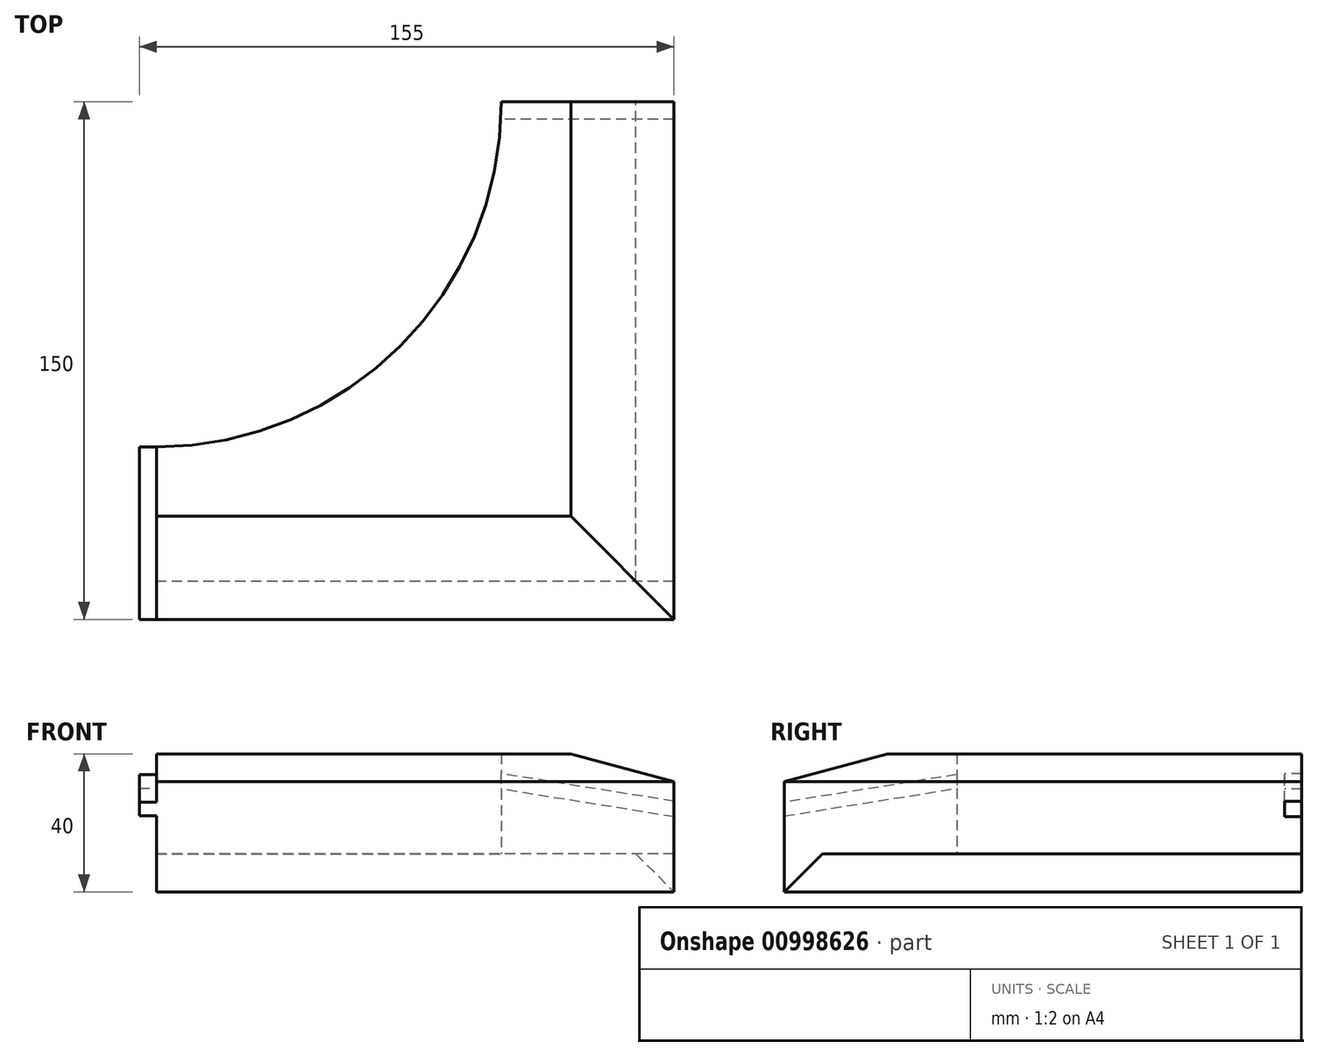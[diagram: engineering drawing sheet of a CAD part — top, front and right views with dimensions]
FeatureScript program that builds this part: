
annotation { "Feature Type Name" : "Feature", "Feature Type Description" : "" }
export const myFeature = defineFeature(function(context is Context, id is Id, definition is map)
    precondition{}
    {
        {
            var Q0;
            Q0=qCreatedBy(makeId("Top.planeOp"),FACE);
            var sketch = newSketch(context, id + "F0", { "sketchPlane" : qUnion([Q0])});
            skLineSegment(sketch, "E0", {"start": v(150, 0) * mm, "end": v(150, -150) * mm});
            skLineSegment(sketch, "E1", {"start": v(150, -150) * mm, "end": v(0, -150) * mm});
            skLineSegment(sketch, "E2", {"start": v(150, 0) * mm, "end": v(100, 0) * mm});
            skLineSegment(sketch, "E3", {"start": v(0, -150) * mm, "end": v(0, -100) * mm});
            skArc(sketch, "E4", {"start": v(0, -100) * mm, "mid": v(70.71, -70.71) * mm, "end": v(100, 0) * mm});
            skSolve(sketch);
        }
        {
            var Q0;
            Q0=makeQuery(id+"F0.imprint","IMPRINT",FACE,{"disambiguationData":[TD([[makeQuery(id+"F0.imprint","IMPRINT",EDGE,{"derivedFrom":sQuery(id+"F0.wireOp",EDGE,"E0")}),-1.0]])]});
            extrude(context, id + "F1", {"entities" : qUnion([Q0]), "depth" : 29 * mm, "offsetDistance" : 25 * mm});
        }
        {
            var Q0;
            Q0=makeQuery(id+"F1.opExtrude","SWEPT_FACE",FACE,{"disambiguationData":[OSD([sQuery(id+"F0.wireOp",EDGE,"E3")])]});
            var sketch = newSketch(context, id + "F2", { "sketchPlane" : qUnion([Q0])});
            skLineSegment(sketch, "E5", {"start": v(120.14, 29) * mm, "end": v(150, 21) * mm});
            skLineSegment(sketch, "E6", {"start": v(150, 21) * mm, "end": v(150, 29) * mm});
            skLineSegment(sketch, "E7", {"start": v(150, 29) * mm, "end": v(120.14, 29) * mm});
            skSolve(sketch);
        }
        {
            var Q0;
            Q0 = qSketchRegion(id + "F2", true);
            extrude(context, id + "F3", {"entities" : qUnion([Q0]), "operationType" : NewBodyOperationType.REMOVE, "endBound" : BoundingType.UP_TO_NEXT, "oppositeDirection" : true, "depth" : 25 * mm, "offsetDistance" : 25 * mm});
        }
        {
            var Q0;
            Q0=makeQuery(id+"F1.opExtrude","SWEPT_FACE",FACE,{"disambiguationData":[OSD([sQuery(id+"F0.wireOp",EDGE,"E2")])]});
            var sketch = newSketch(context, id + "F4", { "sketchPlane" : qUnion([Q0])});
            skLineSegment(sketch, "E8", {"start": v(-150, 29) * mm, "end": v(-120.14, 29) * mm});
            skLineSegment(sketch, "E9", {"start": v(-120.14, 29) * mm, "end": v(-150, 21) * mm});
            skLineSegment(sketch, "E10", {"start": v(-150, 21) * mm, "end": v(-150, 29) * mm});
            skSolve(sketch);
        }
        {
            var Q0;
            Q0 = qSketchRegion(id + "F4", true);
            extrude(context, id + "F5", {"entities" : qUnion([Q0]), "operationType" : NewBodyOperationType.REMOVE, "endBound" : BoundingType.THROUGH_ALL, "oppositeDirection" : true, "depth" : 25 * mm, "offsetDistance" : 25 * mm});
        }
        {
            var Q0;
            Q0=makeQuery(id+"F1.opExtrude","SWEPT_FACE",FACE,{"disambiguationData":[OSD([sQuery(id+"F0.wireOp",EDGE,"E3")])]});
            var sketch = newSketch(context, id + "F6", { "sketchPlane" : qUnion([Q0])});
            skLineSegment(sketch, "E11", {"start": v(100, 23) * mm, "end": v(150, 15) * mm});
            skPoint(sketch, "E11.endSnap0", {"position": v(150, 11) * mm});
            skPoint(sketch, "E11.endSnap1", {"position": v(100, 15) * mm});
            skLineSegment(sketch, "E12", {"start": v(150, 15) * mm, "end": v(150, 11) * mm});
            skLineSegment(sketch, "E13", {"start": v(150, 11) * mm, "end": v(100, 19) * mm});
            skLineSegment(sketch, "E14", {"start": v(100, 19) * mm, "end": v(100, 23) * mm});
            skSolve(sketch);
        }
        {
            var Q0;
            Q0 = qSketchRegion(id + "F6", true);
            extrude(context, id + "F7", {"entities" : qUnion([Q0]), "operationType" : NewBodyOperationType.ADD, "depth" : 5 * mm, "offsetDistance" : 25 * mm});
        }
        {
            var Q0;
            Q0=makeQuery(id+"F1.opExtrude","SWEPT_FACE",FACE,{"disambiguationData":[OSD([sQuery(id+"F0.wireOp",EDGE,"E2")])]});
            var sketch = newSketch(context, id + "F8", { "sketchPlane" : qUnion([Q0])});
            skLineSegment(sketch, "E15", {"start": v(-100, 23.25) * mm, "end": v(-150, 15.25) * mm});
            skLineSegment(sketch, "E16", {"start": v(-100, 18.75) * mm, "end": v(-150, 10.75) * mm});
            skLineSegment(sketch, "E17", {"start": v(-150, 10.75) * mm, "end": v(-150, 15.25) * mm});
            skLineSegment(sketch, "E18", {"start": v(-100, 23.25) * mm, "end": v(-95.06, 24.04) * mm});
            skLineSegment(sketch, "E19", {"start": v(-100, 18.75) * mm, "end": v(-95.06, 19.54) * mm});
            skLineSegment(sketch, "E20", {"start": v(-95.06, 19.54) * mm, "end": v(-95.06, 24.04) * mm});
            skSolve(sketch);
        }
        {
            var Q0;
            Q0 = qSketchRegion(id + "F8", true);
            extrude(context, id + "F9", {"entities" : qUnion([Q0]), "operationType" : NewBodyOperationType.REMOVE, "oppositeDirection" : true, "depth" : 5 * mm, "offsetDistance" : 25 * mm});
        }
        {
            var Q0;
            {var subQ2=sQuery(id+"F0.wireOp",EDGE,"E3");Q0=makeQuery(id+"F7.boolean.opBoolean","SPLIT",FACE,{"disambiguationData":[TD([makeQuery(id+"F7.opExtrude","SWEPT_FACE",FACE,{"disambiguationData":[OSD([sQuery(id+"F6.wireOp",EDGE,"E13")])]})])],"derivedFrom":makeQuery(id+"F1.opExtrude","SWEPT_FACE",FACE,{"disambiguationData":[OSD([subQ2])]})});}
            var sketch = newSketch(context, id + "F10", { "sketchPlane" : qUnion([Q0])});
            skLineSegment(sketch, "E21", {"start": v(150, 0) * mm, "end": v(139, 0) * mm});
            skLineSegment(sketch, "E22", {"start": v(150, 0) * mm, "end": v(150, -11) * mm});
            skLineSegment(sketch, "E23", {"start": v(150, -11) * mm, "end": v(139, 0) * mm});
            skSolve(sketch);
        }
        {
            var Q0;
            Q0=makeQuery(id+"F10.imprint","IMPRINT",FACE,{"disambiguationData":[TD([[makeQuery(id+"F10.imprint","IMPRINT",EDGE,{"derivedFrom":sQuery(id+"F10.wireOp",EDGE,"E21")}),1.0]])]});
            extrude(context, id + "F11", {"entities" : qUnion([Q0]), "operationType" : NewBodyOperationType.ADD, "oppositeDirection" : true, "depth" : 150 * mm, "offsetDistance" : 25 * mm});
        }
        {
            var Q0;
            {var subQ2=sQuery(id+"F0.wireOp",EDGE,"E2");Q0=makeQuery(id+"F9.boolean.opBoolean","SPLIT",FACE,{"disambiguationData":[TD([makeQuery(id+"F9.opExtrude","SWEPT_FACE",FACE,{"disambiguationData":[OSD([sQuery(id+"F8.wireOp",EDGE,"E16"),sQuery(id+"F8.wireOp",EDGE,"E19")])]})])],"derivedFrom":makeQuery(id+"F1.opExtrude","SWEPT_FACE",FACE,{"disambiguationData":[OSD([subQ2])]})});}
            var sketch = newSketch(context, id + "F12", { "sketchPlane" : qUnion([Q0])});
            skLineSegment(sketch, "E24", {"start": v(-150, 0) * mm, "end": v(-150, -11) * mm});
            skLineSegment(sketch, "E25", {"start": v(-150, 0) * mm, "end": v(-139, 0) * mm});
            skLineSegment(sketch, "E26", {"start": v(-139, 0) * mm, "end": v(-150, -11) * mm});
            skSolve(sketch);
        }
        {
            var Q0;
            Q0=makeQuery(id+"F12.imprint","IMPRINT",FACE,{"disambiguationData":[TD([[makeQuery(id+"F12.imprint","IMPRINT",EDGE,{"derivedFrom":sQuery(id+"F12.wireOp",EDGE,"E24")}),1.0]])]});
            var Q1;
            Q1=makeQuery(id+"F1.opExtrude","SWEPT_BODY",BODY,{"disambiguationData":[OSD([sQuery(id+"F0.wireOp",EDGE,"E0"),sQuery(id+"F0.wireOp",EDGE,"E1"),sQuery(id+"F0.wireOp",EDGE,"E2"),sQuery(id+"F0.wireOp",EDGE,"E3"),sQuery(id+"F0.wireOp",EDGE,"E4")])]});
            extrude(context, id + "F13", {"entities" : qUnion([Q0]), "endBound" : BoundingType.UP_TO_BODY, "oppositeDirection" : true, "depth" : 150 * mm, "endBoundEntityBody" : qUnion([Q1]), "offsetDistance" : 25 * mm});
        }
    });
